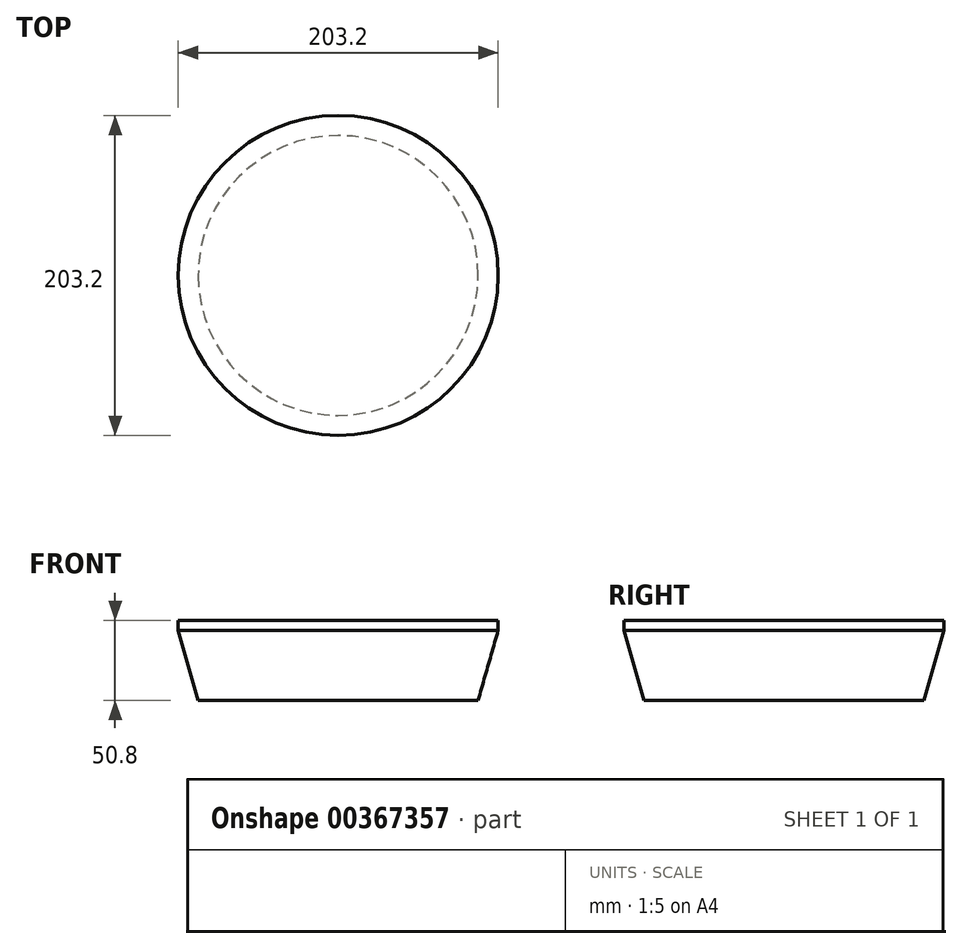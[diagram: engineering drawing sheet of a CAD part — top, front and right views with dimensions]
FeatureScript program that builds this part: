
annotation { "Feature Type Name" : "Feature", "Feature Type Description" : "" }
export const myFeature = defineFeature(function(context is Context, id is Id, definition is map)
    precondition{}
    {
        {
            var Q0;
            Q0=qCreatedBy(makeId("Front.planeOp"),FACE);
            var sketch = newSketch(context, id + "F0", { "sketchPlane" : qUnion([Q0])});
            skLineSegment(sketch, "E0", {"start": v(0, 0) * mm, "end": v(101.6, 0) * mm});
            skLineSegment(sketch, "E1", {"start": v(0, 0) * mm, "end": v(0, -6.35) * mm});
            skLineSegment(sketch, "E2", {"start": v(0, -6.35) * mm, "end": v(101.6, -6.35) * mm});
            skLineSegment(sketch, "E3", {"start": v(101.6, -6.35) * mm, "end": v(101.6, 0) * mm});
            skSolve(sketch);
        }
        {
            var Q0;
            Q0=makeQuery(id+"F0.imprint","IMPRINT",FACE,{"disambiguationData":[TD([[makeQuery(id+"F0.imprint","IMPRINT",EDGE,{"derivedFrom":sQuery(id+"F0.wireOp",EDGE,"E0")}),-1.0]])]});
            var Q1;
            Q1=sQuery(id+"F0.wireOp",EDGE,"E1");
            revolve(context, id + "F1", {"entities" : qUnion([Q0]), "axis" : qUnion([Q1]), "revolveType" : RevolveType.FULL});
        }
        {
            var Q0;
            Q0=qCreatedBy(makeId("Front.planeOp"),FACE);
            var sketch = newSketch(context, id + "F2", { "sketchPlane" : qUnion([Q0])});
            skLineSegment(sketch, "E4", {"start": v(0, 0) * mm, "end": v(0, -50.8) * mm});
            skLineSegment(sketch, "E5", {"start": v(0, -50.8) * mm, "end": v(88.9, -50.8) * mm});
            skLineSegment(sketch, "E6", {"start": v(88.9, -50.8) * mm, "end": v(88.9, -59.73) * mm});
            skLineSegment(sketch, "E7", {"start": v(88.9, -59.73) * mm, "end": v(0, -59.73) * mm});
            skLineSegment(sketch, "E8", {"start": v(0, -59.73) * mm, "end": v(0, -50.8) * mm});
            skSolve(sketch);
        }
        {
            var Q0;
            Q0=makeQuery(id+"F2.imprint","IMPRINT",FACE,{"disambiguationData":[TD([[makeQuery(id+"F2.imprint","IMPRINT",EDGE,{"derivedFrom":sQuery(id+"F2.wireOp",EDGE,"E5")}),-1.0]])]});
            var Q1;
            Q1=sQuery(id+"F2.wireOp",EDGE,"E8");
            revolve(context, id + "F3", {"entities" : qUnion([Q0]), "axis" : qUnion([Q1]), "revolveType" : RevolveType.FULL});
        }
        {
            var Q0;
            Q0=makeQuery(id+"F3.opRevolve","SWEPT_FACE",FACE,{"disambiguationData":[OSD([sQuery(id+"F2.wireOp",EDGE,"E5")])]});
            var Q1;
            Q1=makeQuery(id+"F1.opRevolve","SWEPT_FACE",FACE,{"disambiguationData":[OSD([sQuery(id+"F0.wireOp",EDGE,"E2")])]});
            loft(context, id + "F4", {"sheetProfilesArray" : [{ "sheetProfileEntities" : qUnion([Q0]) }, { "sheetProfileEntities" : qUnion([Q1]) }]});
        }
        {
            var Q0;
            Q0=makeQuery(id+"F3.opRevolve","SWEPT_BODY",BODY,{"disambiguationData":[OSD([sQuery(id+"F2.wireOp",EDGE,"E5"),sQuery(id+"F2.wireOp",EDGE,"E6"),sQuery(id+"F2.wireOp",EDGE,"E7"),sQuery(id+"F2.wireOp",EDGE,"E8")])]});
            deleteBodies(context, id + "F5", {"entities" : qUnion([Q0])});
        }
    });
